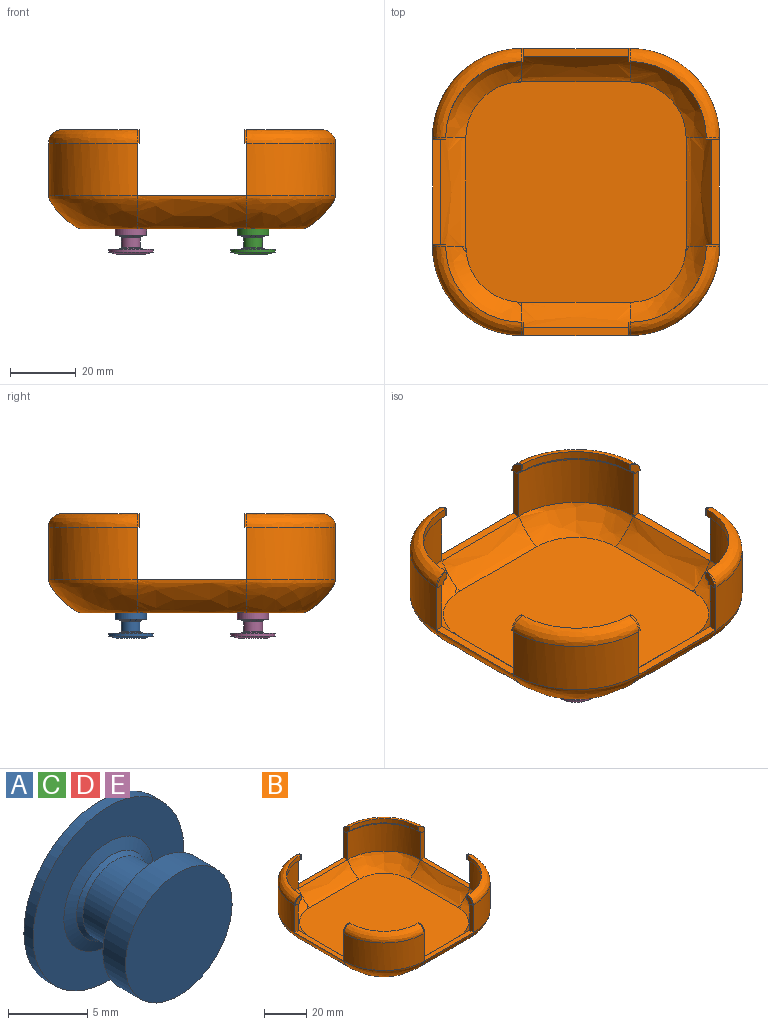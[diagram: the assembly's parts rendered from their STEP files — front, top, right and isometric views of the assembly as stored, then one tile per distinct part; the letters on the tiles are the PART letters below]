
ASSEMBLY  parts=5 mates=4
PART A: 12 faces, bbox 13.4x7.7x13.4 mm
  f0: plane 8.91x8.91mm, normal (0,1,0), area 62.3mm2, adj f11
  f1: plane 9.5x9.5mm, normal (0,-1,0), area 70.8mm2, adj f2
  f2: cylinder r=4.75mm len=9.5mm, axis (0,1,0), area 59.9mm2, adj f1,f3
  f3: plane 9.5x9.5mm, normal (0,1,0), area 26.6mm2, adj f2,f4
  f4: cone r=3.12mm half-angle=61deg, axis (0,-1,0), area 15.6mm2, adj f3,f5
  f5: cone r=2.87mm half-angle=35.2deg, axis (0,-1,0), area 8.1mm2, adj f4,f6
  f6: cylinder r=2.87mm len=5.74mm, axis (0,1,0), area 53.3mm2, adj f5,f7
  f7: cone r=3.14mm half-angle=42.5deg, axis (0,1,0), area 7.5mm2, adj f6,f8
  f8: cone r=3.98mm half-angle=70.6deg, axis (0,1,0), area 19.9mm2, adj f7,f9
  f9: plane 13.44x13.44mm, normal (0,-1,0), area 92mm2, adj f8,f10
  f10: cylinder r=6.72mm len=13.44mm, axis (0,1,0), area 34.6mm2, adj f9,f11
  f11: cone r=4.45mm half-angle=74.9deg, axis (0,-1,0), area 82.3mm2, adj f0,f10
PART B: 102 faces, bbox 92x92x35 mm
  f0: bspline ~33x4mm, area 3.1mm2, adj f1,f5,f41,f99
  f1: bspline ~33x2.5mm, area 1.3mm2, adj f0,f3,f52,f99
  f2: offset ~38x14.57mm, area 357.1mm2, adj f4,f43,f45,f59,f76,f80,f100,f101
  f3: offset ~38x9mm, area 1.2mm2, adj f1,f5,f99
  f4: plane 0.5x0.12mm, normal (-1,0,0), area 0.1mm2, adj f2,f79,f80,f100
  f5: plane 2.5x0.5mm, normal (0,0,-1), area 1.2mm2, adj f0,f3,f79,f99
  f6: bspline ~33x4mm, area 3.1mm2, adj f7,f9,f36,f96
  f7: bspline ~33x2.5mm, area 1.3mm2, adj f6,f8,f48,f96
  f8: offset ~38x9mm, area 1.2mm2, adj f7,f9,f96
  f9: plane 2.5x0.5mm, normal (0,0,-1), area 1.2mm2, adj f6,f8,f68,f96
  f10: plane 0.5x0.12mm, normal (1,0,0), area 0.1mm2, adj f60,f68,f69,f94
  f11: bspline ~33x4mm, area 3.1mm2, adj f13,f18,f37,f93
  f12: bspline ~33x4mm, area 3.1mm2, adj f14,f21,f40,f86
  f13: bspline ~33x2.5mm, area 1.3mm2, adj f11,f16,f50,f93
  f14: bspline ~33x2.5mm, area 1.3mm2, adj f12,f17,f54,f86
  f15: offset ~38x14.57mm, area 357.1mm2, adj f19,f45,f46,f59,f74,f75,f90,f91
  f16: offset ~38x9mm, area 1.2mm2, adj f13,f18,f93
  f17: offset ~38x9mm, area 1.2mm2, adj f14,f21,f86
  f18: plane 2.5x0.5mm, normal (0,0,-1), area 1.2mm2, adj f11,f16,f73,f93
  f19: plane 0.5x0.12mm, normal (0,-1,0), area 0.1mm2, adj f15,f73,f74,f90
  f20: plane 0.5x0.12mm, normal (0,1,0), area 0.1mm2, adj f61,f84,f85,f89
  f21: plane 2.5x0.5mm, normal (0,0,-1), area 1.2mm2, adj f12,f17,f84,f86
  f22: cylinder r=27mm len=27mm, axis (0,0,-1), area 678.6mm2, adj f28,f36,f68,f71
  f23: cylinder r=27mm len=27mm, axis (0,0,-1), area 678.6mm2, adj f32,f40,f66,f84
  f24: cylinder r=27mm len=27mm, axis (0,0,-1), area 678.6mm2, adj f33,f41,f79,f82
  f25: cylinder r=27mm len=27mm, axis (0,0,-1), area 678.6mm2, adj f29,f37,f73,f77
  f26: plane 67.01x67.01mm, normal (0,0,-1), area 4240.7mm2, adj f27,f28,f29,f30,f31,f32,f33,f34
  f27: bspline ~33x10mm, area 483.1mm2, adj f26,f28,f29,f74
  f28: bspline ~27x27mm, area 522.6mm2, adj f22,f26,f27,f30
  f29: bspline ~27x27mm, area 522.6mm2, adj f25,f26,f27,f31
  f30: bspline ~33x10mm, area 483.1mm2, adj f26,f28,f32,f69
  f31: bspline ~33x10mm, area 483.1mm2, adj f26,f29,f33,f80
  f32: bspline ~27x27mm, area 522.6mm2, adj f23,f26,f30,f34
  f33: bspline ~27x27mm, area 522.6mm2, adj f24,f26,f31,f34
  f34: bspline ~33x10mm, area 483.1mm2, adj f26,f32,f33,f85
  f35: bspline ~33x4mm, area 3.1mm2, adj f36,f49,f72,f92
  f36: bspline ~27x27mm, area 250.7mm2, adj f6,f22,f35,f48
  f37: bspline ~27x27mm, area 250.7mm2, adj f11,f25,f39,f50
  f38: bspline ~33x4mm, area 3.1mm2, adj f40,f47,f67,f97
  f39: bspline ~33x4mm, area 3.1mm2, adj f37,f51,f78,f98
  f40: bspline ~27x27mm, area 250.7mm2, adj f12,f23,f38,f54
  f41: bspline ~27x27mm, area 250.7mm2, adj f0,f24,f42,f52
  f42: bspline ~33x4mm, area 3.1mm2, adj f41,f53,f83,f87
  f43: offset ~31.95x31.95mm, area 362.2mm2, adj f2,f57,f59,f61
  f44: offset ~31.95x31.95mm, area 362.2mm2, adj f56,f59,f60,f61
  f45: offset ~31.95x31.95mm, area 362.2mm2, adj f2,f15,f58,f59
  f46: offset ~31.95x31.95mm, area 362.2mm2, adj f15,f55,f59,f60
  f47: bspline ~33x2.5mm, area 1.2mm2, adj f38,f54,f63,f97
  f48: bspline ~23x23mm, area 90.3mm2, adj f7,f36,f49
  f49: bspline ~33x2.5mm, area 1.2mm2, adj f35,f48,f62,f92
  f50: bspline ~23x23mm, area 90.3mm2, adj f13,f37,f51
  f51: bspline ~33x2.5mm, area 1.2mm2, adj f39,f50,f64,f98
  f52: bspline ~23x23mm, area 90.3mm2, adj f1,f41,f53
  f53: bspline ~33x2.5mm, area 1.2mm2, adj f42,f52,f65,f87
  f54: bspline ~23x23mm, area 90.3mm2, adj f14,f40,f47
  f55: cylinder r=24.5mm len=24.5mm, axis (0,0,-1), area 611.3mm2, adj f46,f68,f71
  f56: cylinder r=24.5mm len=24.5mm, axis (0,0,-1), area 611.3mm2, adj f44,f66,f84
  f57: cylinder r=24.5mm len=24.5mm, axis (0,0,-1), area 611.3mm2, adj f43,f79,f82
  f58: cylinder r=24.5mm len=24.5mm, axis (0,0,-1), area 611.3mm2, adj f45,f73,f77
  f59: plane 66.81x66.81mm, normal (0,0,1), area 4213.3mm2, adj f2,f15,f43,f44,f45,f46,f60,f61
  f60: offset ~38x14.57mm, area 357.1mm2, adj f10,f44,f46,f59,f69,f70,f94,f95
  f61: offset ~38x14.57mm, area 357.1mm2, adj f20,f43,f44,f59,f81,f85,f88,f89
  f62: offset ~38x9mm, area 1.2mm2, adj f49,f72,f92
  f63: offset ~38x9mm, area 1.2mm2, adj f47,f67,f97
  f64: offset ~38x9mm, area 1.2mm2, adj f51,f78,f98
  f65: offset ~38x9mm, area 1.2mm2, adj f53,f83,f87
  f66: plane 16x2.5mm, normal (0,-1,0), area 40mm2, adj f23,f56,f67,f69,f70
  f67: plane 2.5x0.5mm, normal (0,0,-1), area 1.2mm2, adj f38,f63,f66,f97
  f68: plane 16x2.5mm, normal (0,1,0), area 40mm2, adj f9,f10,f22,f55,f69
  f69: plane 33x2.54mm, normal (0,0,1), area 83.8mm2, adj f10,f30,f60,f66,f68,f70,f94,f95
  f70: plane 0.5x0.12mm, normal (1,0,0), area 0.1mm2, adj f60,f66,f69,f95
  f71: plane 16x2.5mm, normal (-1,0,0), area 40mm2, adj f22,f55,f72,f74,f75
  f72: plane 2.5x0.5mm, normal (0,0,-1), area 1.2mm2, adj f35,f62,f71,f92
  f73: plane 16x2.5mm, normal (1,0,0), area 40mm2, adj f18,f19,f25,f58,f74
  f74: plane 33x2.54mm, normal (0,0,1), area 83.8mm2, adj f15,f19,f27,f71,f73,f75,f90,f91
  f75: plane 0.5x0.12mm, normal (0,-1,0), area 0.1mm2, adj f15,f71,f74,f91
  f76: plane 0.5x0.12mm, normal (-1,0,0), area 0.1mm2, adj f2,f77,f80,f101
  f77: plane 16x2.5mm, normal (0,1,0), area 40mm2, adj f25,f58,f76,f78,f80
  f78: plane 2.5x0.5mm, normal (0,0,-1), area 1.2mm2, adj f39,f64,f77,f98
  f79: plane 16x2.5mm, normal (0,-1,0), area 40mm2, adj f4,f5,f24,f57,f80
  f80: plane 33x2.54mm, normal (0,0,1), area 83.8mm2, adj f2,f4,f31,f76,f77,f79,f100,f101
  f81: plane 0.5x0.12mm, normal (0,1,0), area 0.1mm2, adj f61,f82,f85,f88
  f82: plane 16x2.5mm, normal (1,0,0), area 40mm2, adj f24,f57,f81,f83,f85
  f83: plane 2.5x0.5mm, normal (0,0,-1), area 1.2mm2, adj f42,f65,f82,f87
  f84: plane 16x2.5mm, normal (-1,0,0), area 40mm2, adj f20,f21,f23,f56,f85
  f85: plane 33x2.54mm, normal (0,0,1), area 83.8mm2, adj f20,f34,f61,f81,f82,f84,f88,f89
  f86: plane 4.2x4.2mm, normal (-1,0,0), area 10.7mm2, adj f12,f14,f17,f21
  f87: plane 4.2x4.2mm, normal (1,0,0), area 10.7mm2, adj f42,f53,f65,f83
  f88: plane 0.13x0.06mm, normal (1,0,0), area 0mm2, adj f61,f81,f85
  f89: plane 0.13x0.06mm, normal (-1,0,0), area 0mm2, adj f20,f61,f85
  f90: plane 0.13x0.06mm, normal (1,0,0), area 0mm2, adj f15,f19,f74
  f91: plane 0.13x0.06mm, normal (-1,0,0), area 0mm2, adj f15,f74,f75
  f92: plane 4.2x4.2mm, normal (-1,0,0), area 10.7mm2, adj f35,f49,f62,f72
  f93: plane 4.2x4.2mm, normal (1,0,0), area 10.7mm2, adj f11,f13,f16,f18
  f94: plane 0.13x0.06mm, normal (0,1,0), area 0mm2, adj f10,f60,f69
  f95: plane 0.13x0.06mm, normal (0,-1,0), area 0mm2, adj f60,f69,f70
  f96: plane 4.2x4.2mm, normal (0,1,0), area 10.7mm2, adj f6,f7,f8,f9
  f97: plane 4.2x4.2mm, normal (0,-1,0), area 10.7mm2, adj f38,f47,f63,f67
  f98: plane 4.2x4.2mm, normal (0,1,0), area 10.7mm2, adj f39,f51,f64,f78
  f99: plane 4.2x4.2mm, normal (0,-1,0), area 10.7mm2, adj f0,f1,f3,f5
  f100: plane 0.13x0.06mm, normal (0,-1,0), area 0mm2, adj f2,f4,f80
  f101: plane 0.13x0.06mm, normal (0,1,0), area 0mm2, adj f2,f76,f80
PART C: same geometry as A
PART D: same geometry as A
PART E: same geometry as A
PLACE A rot(axis=(-1,0,0),90deg) t=(-14.36,41.66,12.25)mm
PLACE B t=(4.16,23.14,16.1)mm
PLACE C rot(axis=(-1,0,0),90deg) t=(22.68,4.61,12.25)mm
PLACE D rot(axis=(-1,0,0),90deg) t=(22.68,41.66,12.25)mm
PLACE E rot(axis=(-1,0,0),90deg) t=(-14.36,4.61,12.25)mm
MATE fastened D.f2 <-> B.f26  axis (0,0,1) through (22.68,41.66,16.1)mm
MATE fastened E.f2 <-> B.f26  axis (0,0,1) through (-14.36,4.61,16.1)mm
MATE fastened A.f2 <-> B.f26  axis (0,0,1) through (-14.36,41.66,16.1)mm
MATE fastened C.f2 <-> B.f26  axis (0,0,1) through (22.68,4.61,16.1)mm
